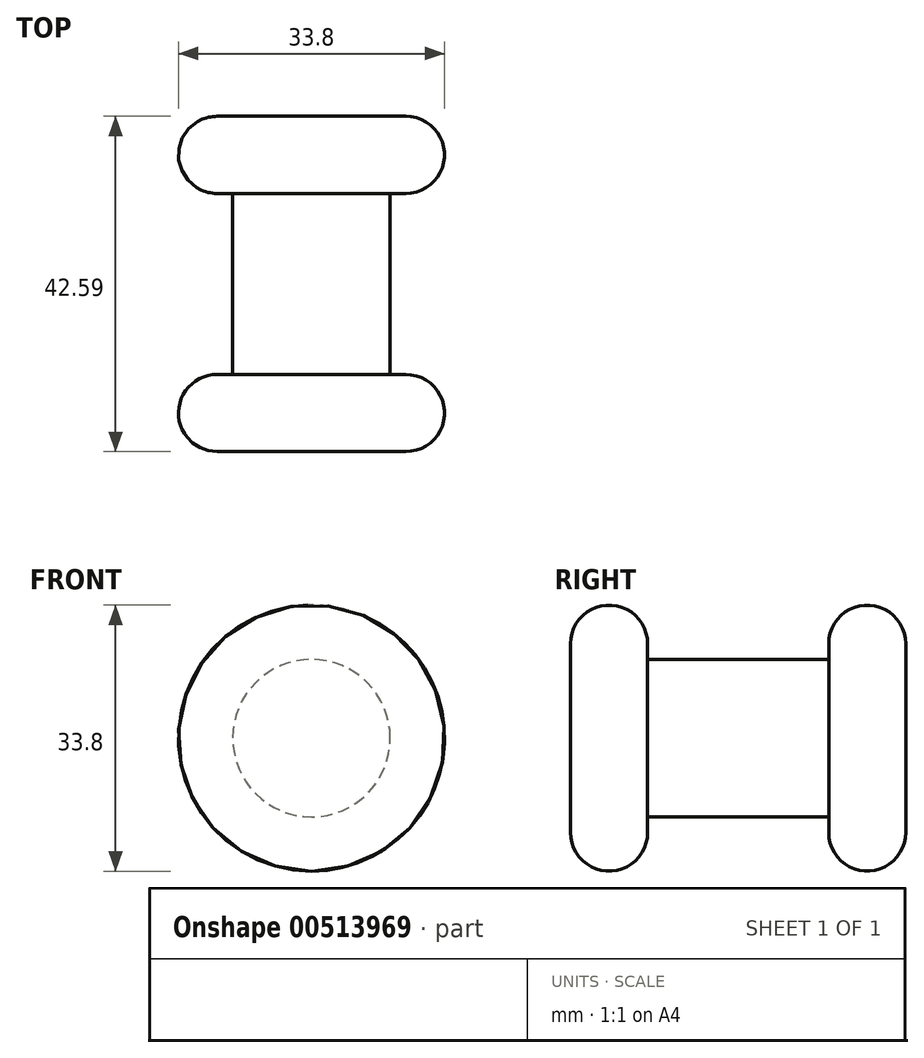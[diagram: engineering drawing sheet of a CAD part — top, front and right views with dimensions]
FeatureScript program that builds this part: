
annotation { "Feature Type Name" : "Feature", "Feature Type Description" : "" }
export const myFeature = defineFeature(function(context is Context, id is Id, definition is map)
    precondition{}
    {
        {
            var Q0;
            Q0=qCreatedBy(makeId("Top.planeOp"),FACE);
            var sketch = newSketch(context, id + "F0", { "sketchPlane" : qUnion([Q0])});
            skLineSegment(sketch, "E0.bottom", {"start": v(0, 0) * mm, "end": v(-12, 0) * mm});
            skLineSegment(sketch, "E0.top", {"start": v(0, 9.8) * mm, "end": v(-12, 9.8) * mm});
            skLineSegment(sketch, "E0.left", {"start": v(0, 0) * mm, "end": v(0, 9.8) * mm});
            skLineSegment(sketch, "E1.bottom", {"start": v(0, 9.8) * mm, "end": v(-10, 9.8) * mm});
            skLineSegment(sketch, "E1.top", {"start": v(0, 32.8) * mm, "end": v(-10, 32.8) * mm});
            skLineSegment(sketch, "E1.left", {"start": v(0, 9.8) * mm, "end": v(0, 32.8) * mm});
            skLineSegment(sketch, "E1.right", {"start": v(-10, 9.8) * mm, "end": v(-10, 32.8) * mm});
            skLineSegment(sketch, "E2.bottom", {"start": v(0, 32.8) * mm, "end": v(-12, 32.8) * mm});
            skLineSegment(sketch, "E2.top", {"start": v(0, 42.6) * mm, "end": v(-12, 42.6) * mm});
            skLineSegment(sketch, "E2.left", {"start": v(0, 32.8) * mm, "end": v(0, 42.6) * mm});
            skArc(sketch, "E3", {"start": v(-12, 42.6) * mm, "mid": v(-16.9, 37.7) * mm, "end": v(-12, 32.8) * mm});
            skArc(sketch, "E4", {"start": v(-12, 9.8) * mm, "mid": v(-16.9, 4.9) * mm, "end": v(-12, 0) * mm});
            skSolve(sketch);
        }
        {
            var Q0;
            Q0 = qSketchRegion(id + "F0", true);
            var Q1;
            Q1=sQuery(id+"F0.wireOp",EDGE,"E1.left");
            revolve(context, id + "F1", {"entities" : qUnion([Q0]), "axis" : qUnion([Q1]), "revolveType" : RevolveType.FULL});
        }
    });
